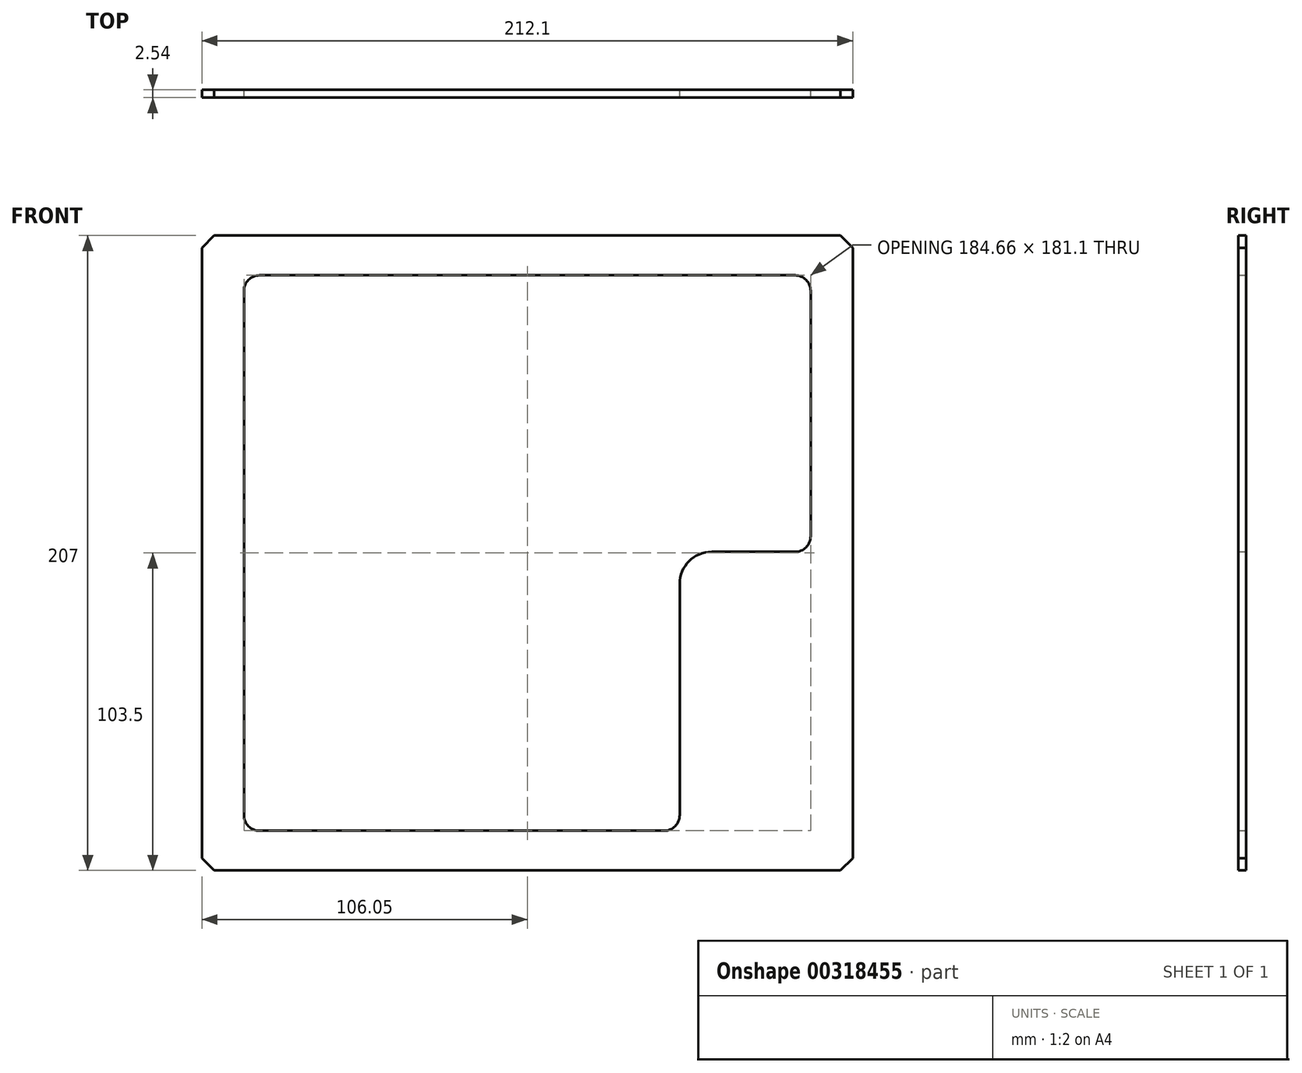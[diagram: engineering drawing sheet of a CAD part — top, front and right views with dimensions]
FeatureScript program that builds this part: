
annotation { "Feature Type Name" : "Feature", "Feature Type Description" : "" }
export const myFeature = defineFeature(function(context is Context, id is Id, definition is map)
    precondition{}
    {
        {
            var Q0;
            Q0=qCreatedBy(makeId("Front.planeOp"),FACE);
            var sketch = newSketch(context, id + "F0", { "sketchPlane" : qUnion([Q0])});
            skLineSegment(sketch, "E0.bottom", {"start": v(-106.04, -103.5) * mm, "end": v(106.05, -103.5) * mm});
            skLineSegment(sketch, "E0.top", {"start": v(-106.05, 103.5) * mm, "end": v(106.04, 103.5) * mm});
            skLineSegment(sketch, "E0.left", {"start": v(-106.04, -103.5) * mm, "end": v(-106.05, 103.5) * mm});
            skLineSegment(sketch, "E0.right", {"start": v(106.05, -103.5) * mm, "end": v(106.04, 103.5) * mm});
            skPoint(sketch, "E0.middle", {"position": v(0, 0) * mm});
            skLineSegment(sketch, "E1", {"start": v(-106.05, 99.55) * mm, "end": v(-102.1, 103.5) * mm});
            skLineSegment(sketch, "E2", {"start": v(-106.04, -99.55) * mm, "end": v(-102.1, -103.5) * mm});
            skLineSegment(sketch, "E3", {"start": v(106.04, -99.55) * mm, "end": v(102.1, -103.5) * mm});
            skLineSegment(sketch, "E4", {"start": v(102.1, 103.5) * mm, "end": v(106.04, 99.55) * mm});
            skLineSegment(sketch, "E5.top", {"start": v(-87.25, 90.55) * mm, "end": v(87.25, 90.55) * mm});
            skLineSegment(sketch, "E5.left", {"start": v(-92.33, -85.47) * mm, "end": v(-92.33, 85.47) * mm});
            skLineSegment(sketch, "E6", {"start": v(-87.25, -90.55) * mm, "end": v(44.58, -90.55) * mm});
            skLineSegment(sketch, "E7", {"start": v(49.66, -85.47) * mm, "end": v(49.66, -10.03) * mm});
            skLineSegment(sketch, "E8", {"start": v(60.07, 0.38) * mm, "end": v(87.25, 0.38) * mm});
            skLineSegment(sketch, "E9", {"start": v(92.33, 5.46) * mm, "end": v(92.33, 85.47) * mm});
            skPoint(sketch, "E10.visualSharp", {"position": v(-92.33, 90.55) * mm});
            skArc(sketch, "E10.filletArc", {"start": v(-87.25, 90.55) * mm, "mid": v(-90.84, 89.06) * mm, "end": v(-92.33, 85.47) * mm});
            skPoint(sketch, "E11.visualSharp", {"position": v(92.33, 90.55) * mm});
            skArc(sketch, "E11.filletArc", {"start": v(92.33, 85.47) * mm, "mid": v(90.84, 89.06) * mm, "end": v(87.25, 90.55) * mm});
            skPoint(sketch, "E12.visualSharp", {"position": v(92.33, 0.38) * mm});
            skArc(sketch, "E12.filletArc", {"start": v(87.25, 0.38) * mm, "mid": v(90.84, 1.87) * mm, "end": v(92.33, 5.46) * mm});
            skPoint(sketch, "E13.visualSharp", {"position": v(49.66, -90.55) * mm});
            skArc(sketch, "E13.filletArc", {"start": v(44.58, -90.55) * mm, "mid": v(48.17, -89.06) * mm, "end": v(49.66, -85.47) * mm});
            skPoint(sketch, "E14.visualSharp", {"position": v(-92.33, -90.55) * mm});
            skArc(sketch, "E14.filletArc", {"start": v(-92.33, -85.47) * mm, "mid": v(-90.84, -89.06) * mm, "end": v(-87.25, -90.55) * mm});
            skPoint(sketch, "E15.visualSharp", {"position": v(49.66, 0.38) * mm});
            skArc(sketch, "E15.filletArc", {"start": v(60.07, 0.38) * mm, "mid": v(52.7, -2.67) * mm, "end": v(49.66, -10.03) * mm});
            skSolve(sketch);
        }
        {
            var Q0;
            {var subQ2=sQuery(id+"F0.wireOp",EDGE,"E1");Q0=makeQuery(id+"F0.imprint","IMPRINT",FACE,{"disambiguationData":[TD([[makeQuery(id+"F0.imprint","IMPRINT",EDGE,{"derivedFrom":subQ2}),-1.0]])]});}
            extrude(context, id + "F1", {"entities" : qUnion([Q0]), "depth" : 2.54 * mm, "offsetDistance" : 25.4 * mm});
        }
    });
